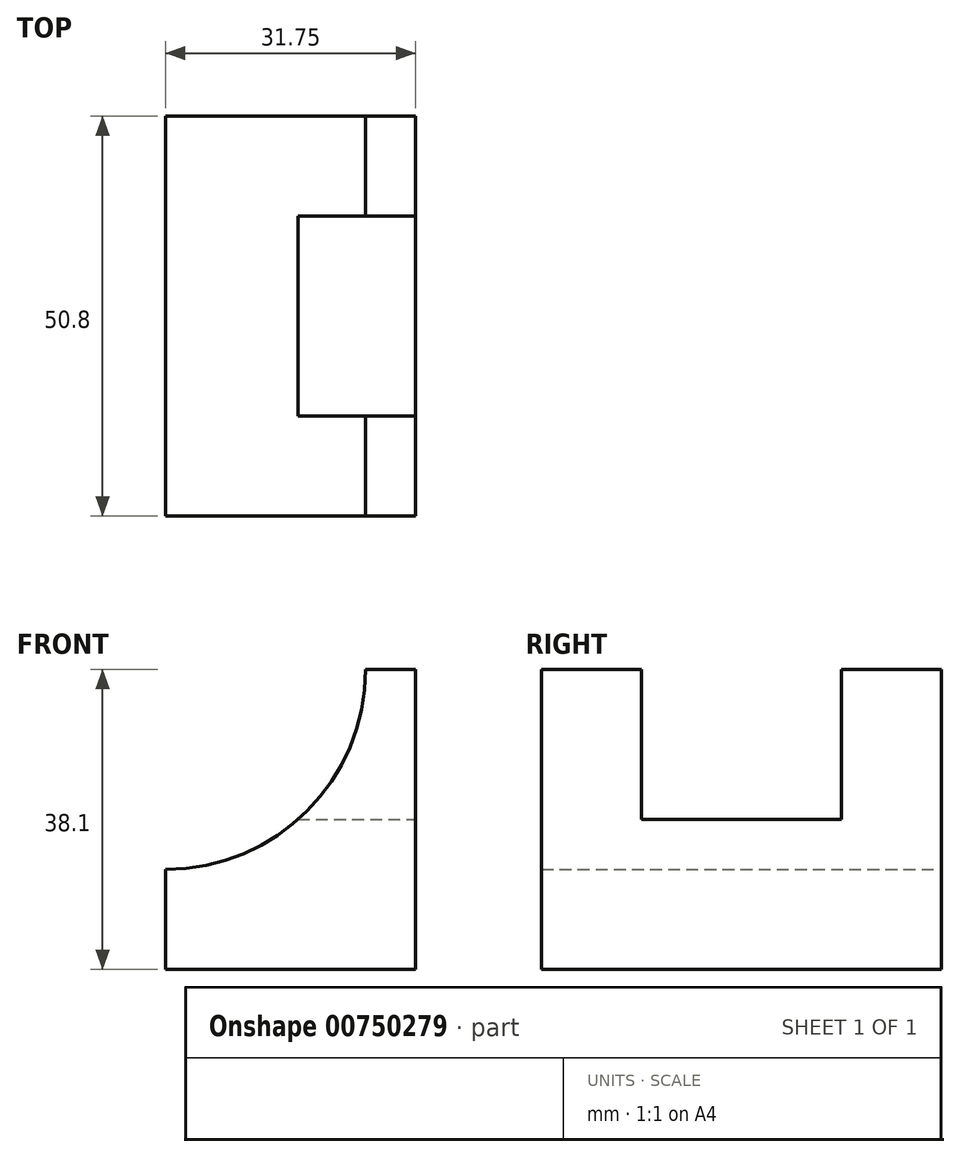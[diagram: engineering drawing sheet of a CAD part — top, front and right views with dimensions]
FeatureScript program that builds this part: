
annotation { "Feature Type Name" : "Feature", "Feature Type Description" : "" }
export const myFeature = defineFeature(function(context is Context, id is Id, definition is map)
    precondition{}
    {
        {
            var Q0;
            Q0=qCreatedBy(makeId("Front.planeOp"),FACE);
            var sketch = newSketch(context, id + "F0", { "sketchPlane" : qUnion([Q0])});
            skLineSegment(sketch, "E0", {"start": v(0, 0) * mm, "end": v(31.75, 0) * mm});
            skLineSegment(sketch, "E1", {"start": v(31.75, 0) * mm, "end": v(31.75, 38.1) * mm});
            skLineSegment(sketch, "E2", {"start": v(31.75, 38.1) * mm, "end": v(25.4, 38.1) * mm});
            skLineSegment(sketch, "E3", {"start": v(0, 0) * mm, "end": v(0, 12.7) * mm});
            skLineSegment(sketch, "E4.bottom", {"start": v(0, 12.7) * mm, "end": v(25.4, 12.7) * mm});
            skLineSegment(sketch, "E4.top", {"start": v(0, 38.1) * mm, "end": v(25.4, 38.1) * mm});
            skLineSegment(sketch, "E4.left", {"start": v(0, 12.7) * mm, "end": v(0, 38.1) * mm});
            skLineSegment(sketch, "E4.right", {"start": v(25.4, 12.7) * mm, "end": v(25.4, 38.1) * mm});
            skArc(sketch, "E5", {"start": v(0, 12.7) * mm, "mid": v(17.96, 20.14) * mm, "end": v(25.4, 38.1) * mm});
            skSolve(sketch);
        }
        {
            var Q0;
            Q0=makeQuery(id+"F0.imprint","IMPRINT",FACE,{"disambiguationData":[TD([[makeQuery(id+"F0.imprint","IMPRINT",EDGE,{"derivedFrom":sQuery(id+"F0.wireOp",EDGE,"E4.bottom")}),1.0]])]});
            var Q1;
            Q1=makeQuery(id+"F0.imprint","IMPRINT",FACE,{"disambiguationData":[TD([[makeQuery(id+"F0.imprint","IMPRINT",EDGE,{"derivedFrom":sQuery(id+"F0.wireOp",EDGE,"E0")}),1.0]])]});
            extrude(context, id + "F1", {"entities" : qUnion([Q0, Q1]), "depth" : 50.8 * mm, "offsetDistance" : 25.4 * mm});
        }
        {
            var Q0;
            Q0=makeQuery(id+"F1.opExtrude","SWEPT_FACE",FACE,{"disambiguationData":[OSD([sQuery(id+"F0.wireOp",EDGE,"E1")])]});
            var sketch = newSketch(context, id + "F2", { "sketchPlane" : qUnion([Q0])});
            skLineSegment(sketch, "E6.bottom", {"start": v(-38.1, 38.1) * mm, "end": v(-12.7, 38.1) * mm});
            skLineSegment(sketch, "E6.top", {"start": v(-38.1, 19.05) * mm, "end": v(-12.7, 19.05) * mm});
            skLineSegment(sketch, "E6.left", {"start": v(-38.1, 38.1) * mm, "end": v(-38.1, 19.05) * mm});
            skLineSegment(sketch, "E6.right", {"start": v(-12.7, 38.1) * mm, "end": v(-12.7, 19.05) * mm});
            skSolve(sketch);
        }
        {
            var Q0;
            Q0=makeQuery(id+"F2.imprint","IMPRINT",FACE,{"disambiguationData":[TD([[makeQuery(id+"F2.imprint","IMPRINT",EDGE,{"derivedFrom":sQuery(id+"F2.wireOp",EDGE,"E6.bottom")}),-1.0]])]});
            extrude(context, id + "F3", {"entities" : qUnion([Q0]), "operationType" : NewBodyOperationType.REMOVE, "oppositeDirection" : true, "depth" : 25.4 * mm, "offsetDistance" : 25.4 * mm});
        }
    });
